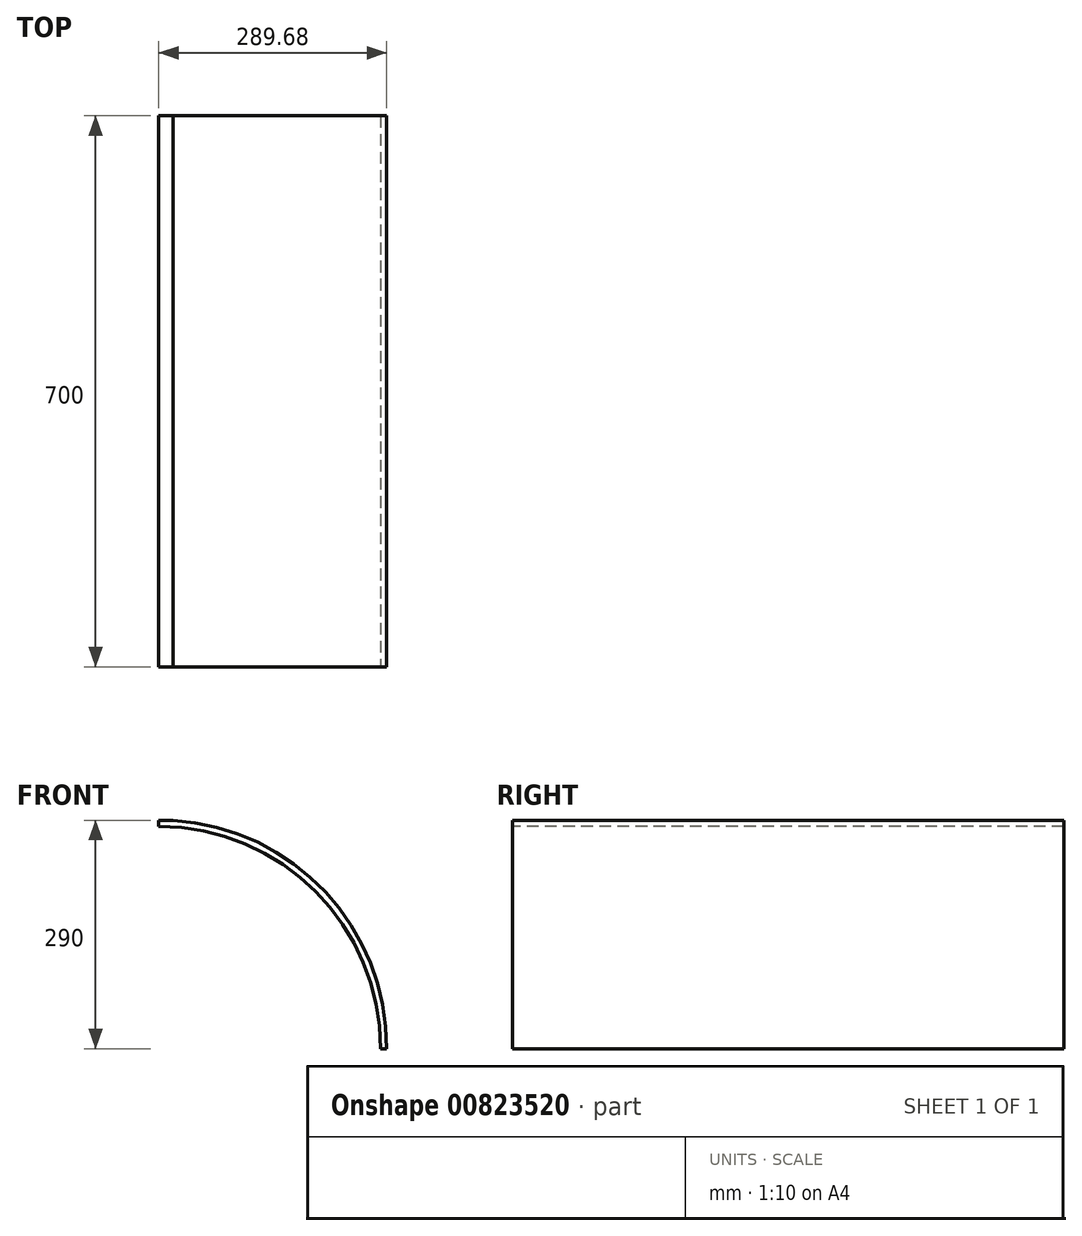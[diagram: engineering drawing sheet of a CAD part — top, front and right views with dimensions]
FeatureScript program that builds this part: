
annotation { "Feature Type Name" : "Feature", "Feature Type Description" : "" }
export const myFeature = defineFeature(function(context is Context, id is Id, definition is map)
    precondition{}
    {
        {
            var Q0;
            Q0=qCreatedBy(makeId("Front.planeOp"),FACE);
            var sketch = newSketch(context, id + "F0", { "sketchPlane" : qUnion([Q0])});
            skLineSegment(sketch, "E0", {"start": v(0, 0) * mm, "end": v(290, 0) * mm});
            skLineSegment(sketch, "E1", {"start": v(290, 0) * mm, "end": v(290, 290) * mm});
            skLineSegment(sketch, "E2", {"start": v(290, 290) * mm, "end": v(0, 290) * mm});
            skLineSegment(sketch, "E3", {"start": v(0, 290) * mm, "end": v(0, 0) * mm});
            skSolve(sketch);
        }
        {
            var Q0;
            Q0 = qSketchRegion(id + "F0", true);
            extrude(context, id + "F1", {"entities" : qUnion([Q0]), "depth" : 700 * mm, "offsetDistance" : 25 * mm});
        }
        {
            var Q0;
            Q0=makeQuery(id+"F0.imprint","IMPRINT",FACE,{"disambiguationData":[TD([[makeQuery(id+"F0.imprint","IMPRINT",EDGE,{"derivedFrom":sQuery(id+"F0.wireOp",EDGE,"E0")}),1.0]])]});
            var sketch = newSketch(context, id + "F2", { "sketchPlane" : qUnion([Q0])});
            skArc(sketch, "E4", {"start": v(289.68, 0) * mm, "mid": v(205.4, 205.65) * mm, "end": v(0, 290.52) * mm});
            skSolve(sketch);
        }
        {
            var Q0;
            {var subQ5=makeQuery(id+"F0.imprint","IMPRINT",EDGE,{"derivedFrom":sQuery(id+"F0.wireOp",EDGE,"E1")});Q0=makeQuery(id+"F2.imprint","IMPRINT",FACE,{"disambiguationData":[TD([[makeQuery(id+"F2.imprint","IMPRINT",EDGE,{"derivedFrom":subQ5}),1.0]])]});}
            extrude(context, id + "F3", {"entities" : qUnion([Q0]), "operationType" : NewBodyOperationType.REMOVE, "depth" : 795 * mm, "offsetDistance" : 25 * mm});
        }
        {
            var Q0;
            Q0=makeQuery(id+"F1.opExtrude","CAP_FACE",FACE,{"disambiguationData":[OSD([sQuery(id+"F0.wireOp",EDGE,"E0"),sQuery(id+"F0.wireOp",EDGE,"E1"),sQuery(id+"F0.wireOp",EDGE,"E2"),sQuery(id+"F0.wireOp",EDGE,"E3")])],"isStart":false});
            var sketch = newSketch(context, id + "F4", { "sketchPlane" : qUnion([Q0])});
            skArc(sketch, "E5", {"start": v(282.12, 0) * mm, "mid": v(199.48, 199.53) * mm, "end": v(0, 282.28) * mm});
            skSolve(sketch);
        }
        {
            var Q0;
            {var subQ0=sQuery(id+"F4.wireOp",EDGE,"E5");Q0=makeQuery(id+"F4.imprint","IMPRINT",FACE,{"disambiguationData":[TD([[makeQuery(id+"F4.imprint","IMPRINT",EDGE,{"derivedFrom":subQ0}),1.0]])]});}
            extrude(context, id + "F5", {"entities" : qUnion([Q0]), "operationType" : NewBodyOperationType.REMOVE, "oppositeDirection" : true, "depth" : 770 * mm, "offsetDistance" : 25 * mm});
        }
    });
